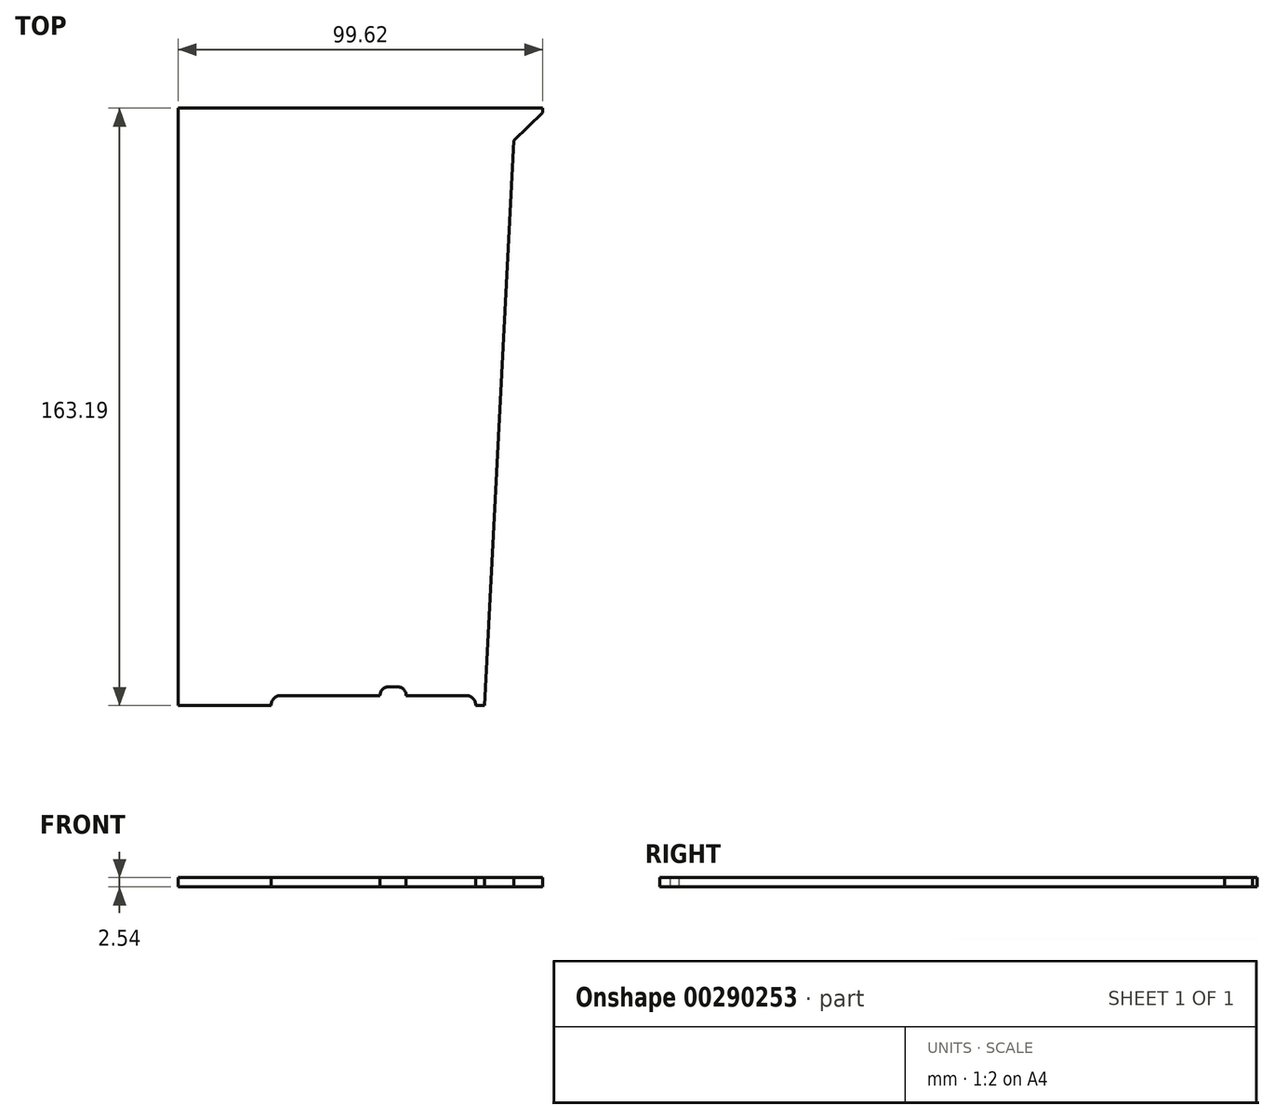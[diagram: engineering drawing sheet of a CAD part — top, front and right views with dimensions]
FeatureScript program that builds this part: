
annotation { "Feature Type Name" : "Feature", "Feature Type Description" : "" }
export const myFeature = defineFeature(function(context is Context, id is Id, definition is map)
    precondition{}
    {
        {
            var Q0;
            Q0=qCreatedBy(makeId("Top.planeOp"),FACE);
            var sketch = newSketch(context, id + "F0", { "sketchPlane" : qUnion([Q0])});
            skLineSegment(sketch, "E0", {"start": v(0, 0) * mm, "end": v(0, -163.2) * mm});
            skLineSegment(sketch, "E1", {"start": v(0, -163.2) * mm, "end": v(25.4, -163.2) * mm});
            skArc(sketch, "E2", {"start": v(28.18, -160.42) * mm, "mid": v(26.21, -161.23) * mm, "end": v(25.4, -163.2) * mm});
            skArc(sketch, "E3", {"start": v(57.55, -158.04) * mm, "mid": v(55.86, -158.73) * mm, "end": v(55.17, -160.42) * mm});
            skArc(sketch, "E4", {"start": v(62.3, -160.42) * mm, "mid": v(61.61, -158.73) * mm, "end": v(59.93, -158.04) * mm});
            skArc(sketch, "E5", {"start": v(81.36, -163.2) * mm, "mid": v(80.55, -161.23) * mm, "end": v(78.58, -160.42) * mm});
            skLineSegment(sketch, "E6", {"start": v(28.18, -160.42) * mm, "end": v(55.17, -160.42) * mm});
            skLineSegment(sketch, "E7", {"start": v(57.55, -158.04) * mm, "end": v(59.93, -158.04) * mm});
            skLineSegment(sketch, "E8", {"start": v(62.3, -160.42) * mm, "end": v(78.58, -160.42) * mm});
            skLineSegment(sketch, "E9", {"start": v(0, 0) * mm, "end": v(99.62, 0) * mm});
            skLineSegment(sketch, "E10", {"start": v(99.62, 0) * mm, "end": v(99.62, -1.27) * mm});
            skLineSegment(sketch, "E11", {"start": v(99.62, -1.27) * mm, "end": v(91.68, -8.89) * mm});
            skLineSegment(sketch, "E12", {"start": v(91.68, -8.89) * mm, "end": v(83.74, -163.2) * mm});
            skLineSegment(sketch, "E13", {"start": v(83.74, -163.2) * mm, "end": v(81.36, -163.2) * mm});
            skSolve(sketch);
        }
        {
            var Q0;
            Q0=makeQuery(id+"F0.imprint","IMPRINT",FACE,{"disambiguationData":[TD([[makeQuery(id+"F0.imprint","IMPRINT",EDGE,{"derivedFrom":sQuery(id+"F0.wireOp",EDGE,"E0")}),1.0]])]});
            extrude(context, id + "F1", {"entities" : qUnion([Q0]), "depth" : 2.54 * mm});
        }
    });
